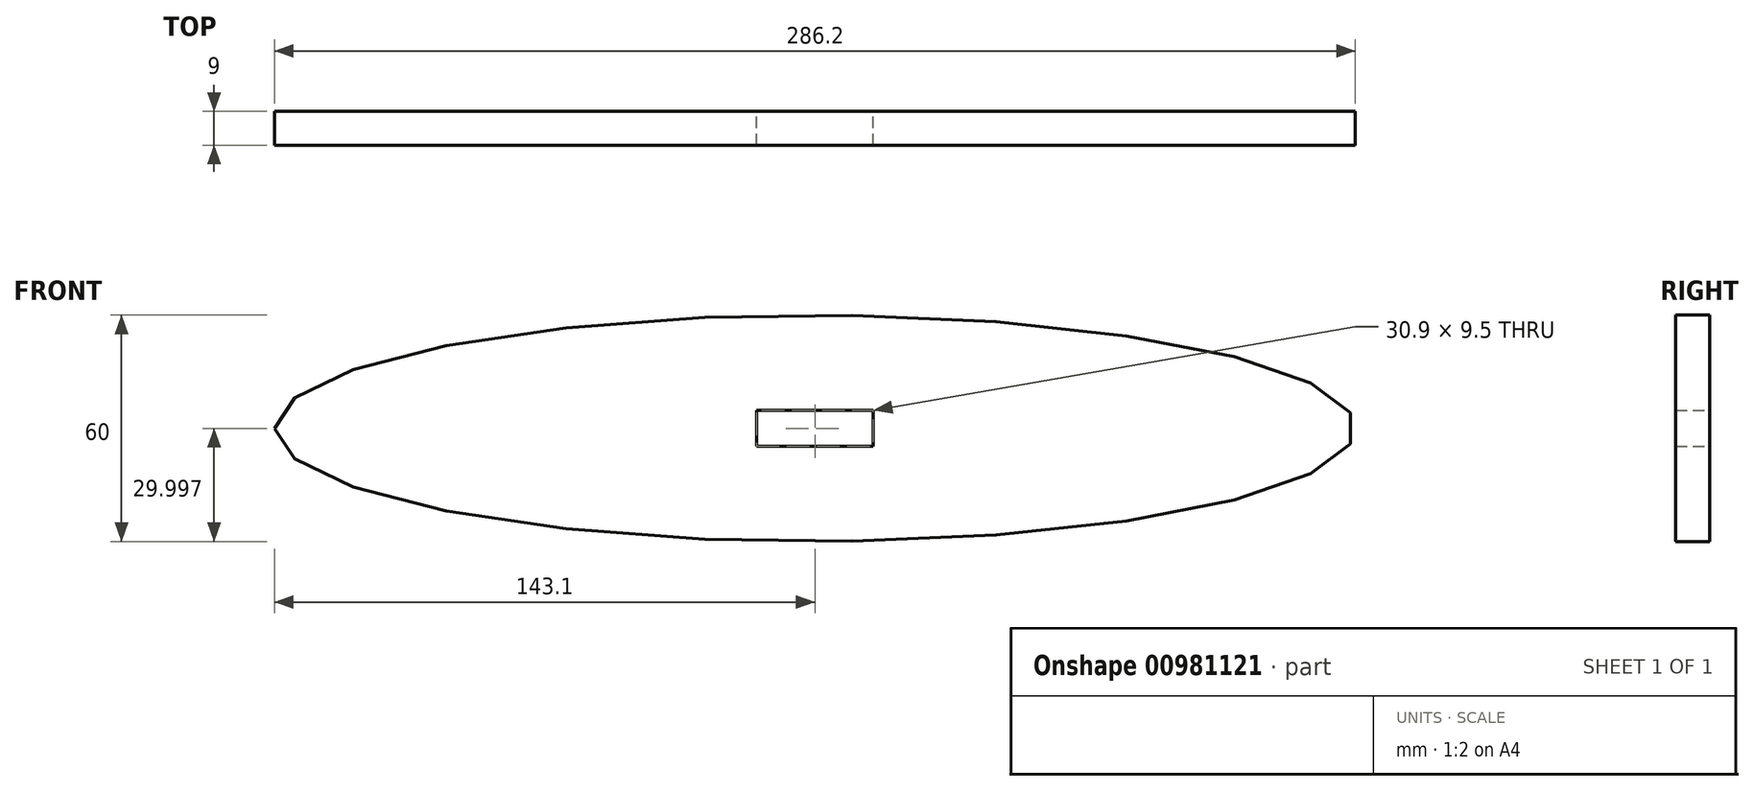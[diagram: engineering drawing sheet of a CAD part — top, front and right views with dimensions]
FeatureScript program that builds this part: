
annotation { "Feature Type Name" : "Feature", "Feature Type Description" : "" }
export const myFeature = defineFeature(function(context is Context, id is Id, definition is map)
    precondition{}
    {
        {
            var Q0;
            Q0=qCreatedBy(makeId("Front.planeOp"),FACE);
            var sketch = newSketch(context, id + "F0", { "sketchPlane" : qUnion([Q0])});
            skEllipse(sketch, "E0", {"center": v(0, -95.35) * mm, "majorRadius": 143.1 * mm, "minorRadius": 30 * mm, "majorAxis": v(-1, 0)});
            skLineSegment(sketch, "E1", {"start": v(15.45, -100.1) * mm, "end": v(-15.45, -100.1) * mm});
            skLineSegment(sketch, "E2", {"start": v(15.45, -90.6) * mm, "end": v(-15.45, -90.6) * mm});
            skLineSegment(sketch, "E3", {"start": v(-15.45, -90.6) * mm, "end": v(-15.45, -100.1) * mm});
            skLineSegment(sketch, "E4", {"start": v(15.45, -90.6) * mm, "end": v(15.45, -100.1) * mm});
            skSolve(sketch);
        }
        {
            var Q0;
            Q0=makeQuery(id+"F0.imprint","IMPRINT",FACE,{"disambiguationData":[TD([[makeQuery(id+"F0.imprint","IMPRINT",EDGE,{"derivedFrom":sQuery(id+"F0.wireOp",EDGE,"E0")}),1.0]])]});
            extrude(context, id + "F1", {"entities" : qUnion([Q0]), "endBound" : BoundingType.SYMMETRIC, "depth" : 9 * mm, "offsetDistance" : 25 * mm});
        }
    });
